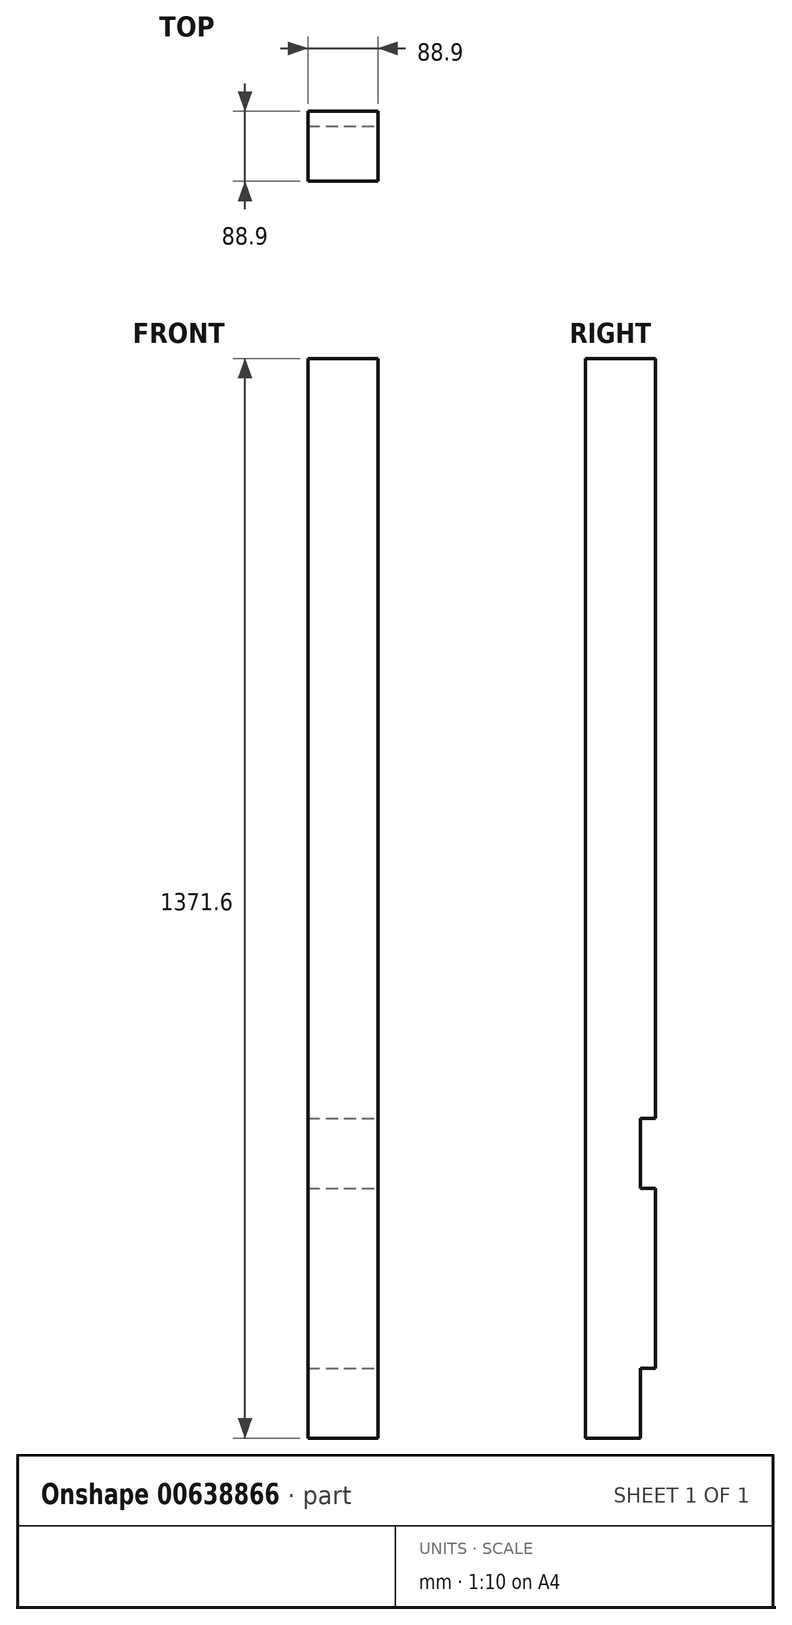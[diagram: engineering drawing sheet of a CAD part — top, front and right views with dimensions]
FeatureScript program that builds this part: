
annotation { "Feature Type Name" : "Feature", "Feature Type Description" : "" }
export const myFeature = defineFeature(function(context is Context, id is Id, definition is map)
    precondition{}
    {
        {
            var Q0;
            Q0=qCreatedBy(makeId("Top.planeOp"),FACE);
            var sketch = newSketch(context, id + "F0", { "sketchPlane" : qUnion([Q0])});
            skLineSegment(sketch, "E0.bottom", {"start": v(44.45, 44.45) * mm, "end": v(-44.45, 44.45) * mm});
            skLineSegment(sketch, "E0.top", {"start": v(44.45, -44.45) * mm, "end": v(-44.45, -44.45) * mm});
            skLineSegment(sketch, "E0.left", {"start": v(44.45, 44.45) * mm, "end": v(44.45, -44.45) * mm});
            skLineSegment(sketch, "E0.right", {"start": v(-44.45, 44.45) * mm, "end": v(-44.45, -44.45) * mm});
            skPoint(sketch, "E0.middle", {"position": v(0, 0) * mm});
            skSolve(sketch);
        }
        {
            var Q0;
            Q0 = qSketchRegion(id + "F0", true);
            extrude(context, id + "F1", {"entities" : qUnion([Q0]), "depth" : 1371.6 * mm, "offsetDistance" : 25.4 * mm});
        }
        {
            var Q0;
            Q0=makeQuery(id+"F1.opExtrude","SWEPT_FACE",FACE,{"disambiguationData":[OSD([sQuery(id+"F0.wireOp",EDGE,"E0.left")])]});
            var sketch = newSketch(context, id + "F2", { "sketchPlane" : qUnion([Q0])});
            skLineSegment(sketch, "E1.bottom", {"start": v(44.45, 0) * mm, "end": v(25.4, 0) * mm});
            skLineSegment(sketch, "E1.top", {"start": v(44.45, 88.9) * mm, "end": v(25.4, 88.9) * mm});
            skLineSegment(sketch, "E1.left", {"start": v(44.45, 0) * mm, "end": v(44.45, 88.9) * mm});
            skLineSegment(sketch, "E1.right", {"start": v(25.4, 0) * mm, "end": v(25.4, 88.9) * mm});
            skLineSegment(sketch, "E2.bottom", {"start": v(44.45, 317.5) * mm, "end": v(25.4, 317.5) * mm});
            skLineSegment(sketch, "E2.top", {"start": v(44.45, 406.4) * mm, "end": v(25.4, 406.4) * mm});
            skLineSegment(sketch, "E2.left", {"start": v(44.45, 317.5) * mm, "end": v(44.45, 406.4) * mm});
            skLineSegment(sketch, "E2.right", {"start": v(25.4, 317.5) * mm, "end": v(25.4, 406.4) * mm});
            skSolve(sketch);
        }
        {
            var Q0;
            Q0=makeQuery(id+"F2.imprint","IMPRINT",FACE,{"disambiguationData":[TD([[makeQuery(id+"F2.imprint","IMPRINT",EDGE,{"derivedFrom":sQuery(id+"F2.wireOp",EDGE,"E2.bottom")}),-1.0]])]});
            var Q1;
            Q1=makeQuery(id+"F2.imprint","IMPRINT",FACE,{"disambiguationData":[TD([[makeQuery(id+"F2.imprint","IMPRINT",EDGE,{"derivedFrom":sQuery(id+"F2.wireOp",EDGE,"E1.bottom")}),-1.0]])]});
            extrude(context, id + "F3", {"entities" : qUnion([Q0, Q1]), "operationType" : NewBodyOperationType.REMOVE, "endBound" : BoundingType.UP_TO_NEXT, "oppositeDirection" : true, "depth" : 25.4 * mm, "offsetDistance" : 25.4 * mm});
        }
    });
